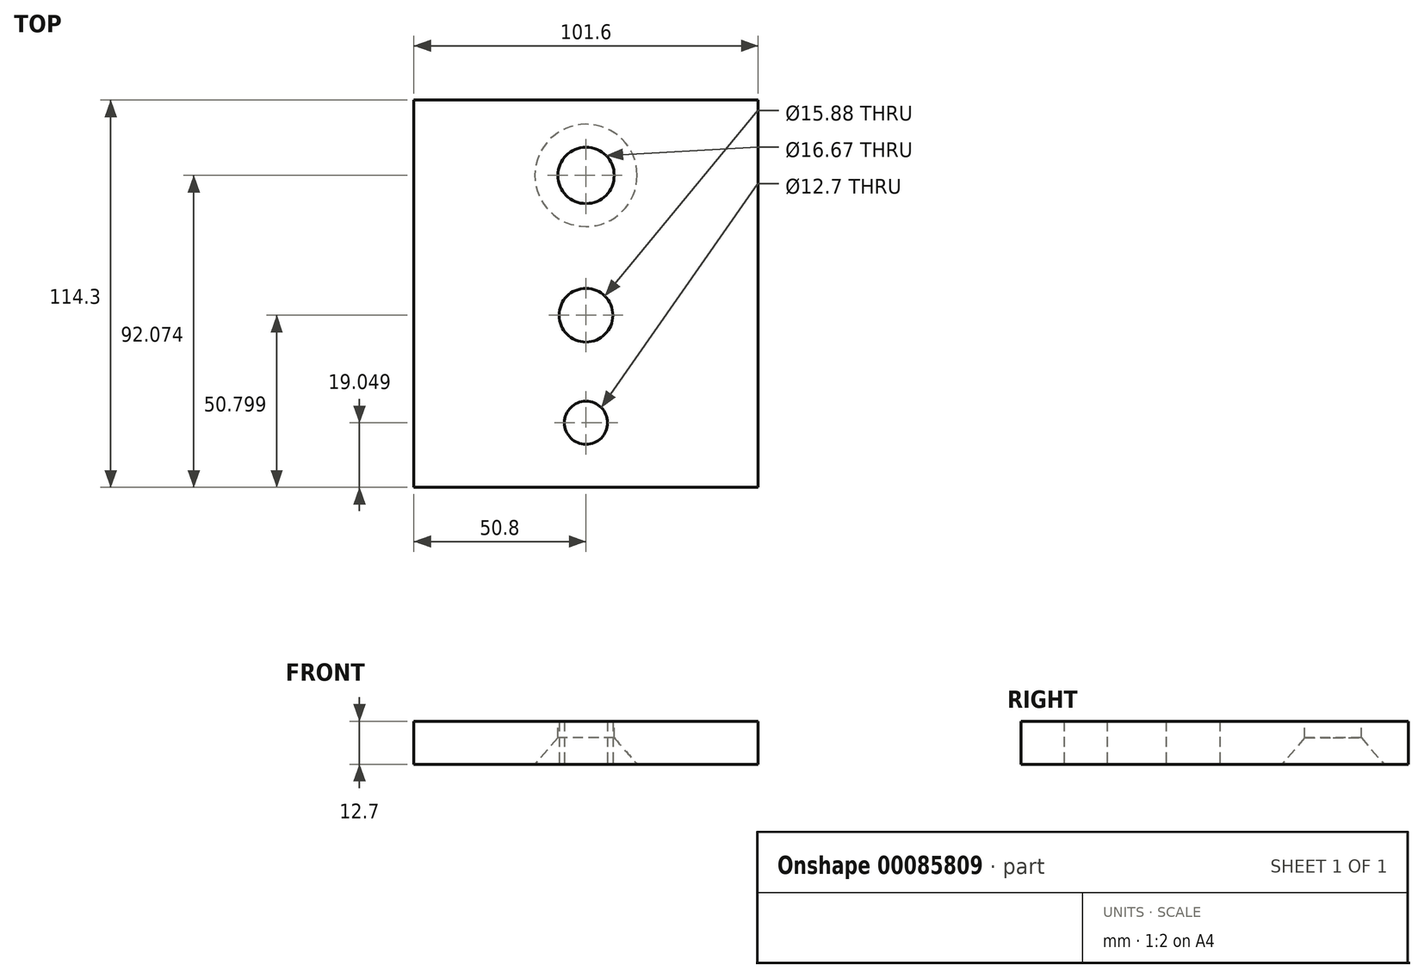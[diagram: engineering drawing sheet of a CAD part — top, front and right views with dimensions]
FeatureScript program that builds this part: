
annotation { "Feature Type Name" : "Feature", "Feature Type Description" : "" }
export const myFeature = defineFeature(function(context is Context, id is Id, definition is map)
    precondition{}
    {
        {
            var Q0;
            Q0=qCreatedBy(makeId("Top.planeOp"),FACE);
            var sketch = newSketch(context, id + "F0", { "sketchPlane" : qUnion([Q0])});
            skPoint(sketch, "E0", {"position": v(-53.4, 28.23) * mm});
            skPoint(sketch, "E1", {"position": v(-53.4, 25.06) * mm});
            skPoint(sketch, "E2", {"position": v(-53.4, 53.63) * mm});
            skPoint(sketch, "E3", {"position": v(-53.4, 12.36) * mm});
            skPoint(sketch, "E4", {"position": v(-53.4, -19.4) * mm});
            skPoint(sketch, "E5", {"position": v(-92.66, 25.06) * mm});
            skLineSegment(sketch, "E6", {"start": v(-7.45, 12.36) * mm, "end": v(-37.08, 12.36) * mm});
            skPoint(sketch, "E7", {"position": v(-23.18, 2.59) * mm});
            skPoint(sketch, "E8", {"position": v(-85.14, 12.36) * mm});
            skPoint(sketch, "E9", {"position": v(-78.42, -7.18) * mm});
            skPoint(sketch, "E10", {"position": v(-20.86, 37.76) * mm});
            skPoint(sketch, "E11", {"position": v(-12.12, 12.36) * mm});
            skLineSegment(sketch, "E12", {"start": v(-2.6, 12.36) * mm, "end": v(-2.6, 63.16) * mm});
            skLineSegment(sketch, "E13", {"start": v(-104.2, 63.16) * mm, "end": v(-104.2, -38.44) * mm});
            skLineSegment(sketch, "E14", {"start": v(-104.2, -38.44) * mm, "end": v(-2.6, -38.44) * mm});
            skLineSegment(sketch, "E15", {"start": v(-2.6, -38.44) * mm, "end": v(-2.6, 63.16) * mm});
            skCircle(sketch, "E16", {"center": v(-53.4, 53.63) * mm, "radius": 1.27 * mm});
            skCircle(sketch, "E17", {"center": v(-92.66, 25.06) * mm, "radius": 1.27 * mm});
            skCircle(sketch, "E18", {"center": v(-85.14, 12.36) * mm, "radius": 1.27 * mm});
            skCircle(sketch, "E19", {"center": v(-78.42, -7.18) * mm, "radius": 1.27 * mm});
            skCircle(sketch, "E20", {"center": v(-53.4, -19.4) * mm, "radius": 1.27 * mm});
            skCircle(sketch, "E21", {"center": v(-23.18, 2.59) * mm, "radius": 1.27 * mm});
            skCircle(sketch, "E22", {"center": v(-12.12, 12.36) * mm, "radius": 1.27 * mm});
            skCircle(sketch, "E23", {"center": v(-20.86, 37.76) * mm, "radius": 1.27 * mm});
            skCircle(sketch, "E24", {"center": v(-53.4, 12.36) * mm, "radius": 1.27 * mm});
            skLineSegment(sketch, "E25", {"start": v(-104.2, 75.86) * mm, "end": v(-2.6, 75.86) * mm});
            skLineSegment(sketch, "E26", {"start": v(-2.6, 63.16) * mm, "end": v(-2.6, 75.86) * mm});
            skLineSegment(sketch, "E27", {"start": v(-104.2, 63.16) * mm, "end": v(-104.2, 75.86) * mm});
            skSolve(sketch);
        }
        {
            var Q0;
            {var subQ0=sQuery(id+"F0.wireOp",EDGE,"oErOf9V9-PG69-BVOV-e9zF-uZxeaokeRpua");Q0=makeQuery(id+"F0.imprint","IMPRINT",FACE,{"disambiguationData":[TD([[makeQuery(id+"F0.imprint","IMPRINT",EDGE,{"derivedFrom":subQ0}),1.0]])]});}
            var Q1;
            Q1=makeQuery(id+"F0.imprint","IMPRINT",FACE,{"disambiguationData":[TD([[makeQuery(id+"F0.imprint","IMPRINT",EDGE,{"derivedFrom":sQuery(id+"F0.wireOp",EDGE,"E13")}),1.0]])]});
            var Q2;
            Q2=makeQuery(id+"F0.imprint","IMPRINT",FACE,{"disambiguationData":[TD([[makeQuery(id+"F0.imprint","IMPRINT",EDGE,{"derivedFrom":sQuery(id+"F0.wireOp",EDGE,"E17")}),1.0]])]});
            var Q3;
            Q3=makeQuery(id+"F0.imprint","IMPRINT",FACE,{"disambiguationData":[TD([[makeQuery(id+"F0.imprint","IMPRINT",EDGE,{"derivedFrom":sQuery(id+"F0.wireOp",EDGE,"E18")}),1.0]])]});
            var Q4;
            Q4=makeQuery(id+"F0.imprint","IMPRINT",FACE,{"disambiguationData":[TD([[makeQuery(id+"F0.imprint","IMPRINT",EDGE,{"derivedFrom":sQuery(id+"F0.wireOp",EDGE,"E19")}),1.0]])]});
            var Q5;
            Q5=makeQuery(id+"F0.imprint","IMPRINT",FACE,{"disambiguationData":[TD([[makeQuery(id+"F0.imprint","IMPRINT",EDGE,{"derivedFrom":sQuery(id+"F0.wireOp",EDGE,"E21")}),1.0]])]});
            var Q6;
            Q6=makeQuery(id+"F0.imprint","IMPRINT",FACE,{"disambiguationData":[TD([[makeQuery(id+"F0.imprint","IMPRINT",EDGE,{"derivedFrom":sQuery(id+"F0.wireOp",EDGE,"E23")}),1.0]])]});
            var Q7;
            {var subQ0=sQuery(id+"F0.wireOp",EDGE,"E22");var subQ1=sQuery(id+"F0.wireOp",EDGE,"E6");var subQ2=makeQuery(id+"F0.imprint","INTERSECT",VERTEX,{"disambiguationData":[OD(0.0)],"derivedFrom":[subQ1,subQ0]});Q7=makeQuery(id+"F0.imprint","IMPRINT",FACE,{"disambiguationData":[TD([[makeQuery(id+"F0.imprint","IMPRINT",EDGE,{"disambiguationData":[TD([[subQ2,1.0]])],"derivedFrom":subQ1}),1.0]])]});}
            var Q8;
            {var subQ0=sQuery(id+"F0.wireOp",EDGE,"E22");var subQ1=sQuery(id+"F0.wireOp",EDGE,"E6");var subQ2=makeQuery(id+"F0.imprint","INTERSECT",VERTEX,{"disambiguationData":[OD(0.0)],"derivedFrom":[subQ1,subQ0]});Q8=makeQuery(id+"F0.imprint","IMPRINT",FACE,{"disambiguationData":[TD([[makeQuery(id+"F0.imprint","IMPRINT",EDGE,{"disambiguationData":[TD([[subQ2,1.0]])],"derivedFrom":subQ1}),-1.0]])]});}
            extrude(context, id + "F1", {"entities" : qUnion([Q0, Q1, Q2, Q3, Q4, Q5, Q6, Q7, Q8]), "depth" : 12.7 * mm, "offsetDistance" : 25.4 * mm});
        }
        {
            var Q0;
            Q0=makeQuery(id+"F1.opExtrude","CAP_FACE",FACE,{"disambiguationData":[OSD([sQuery(id+"F0.wireOp",EDGE,"oErOf9V9-PG69-BVOV-e9zF-uZxeaokeRpua"),sQuery(id+"F0.wireOp",EDGE,"E13"),sQuery(id+"F0.wireOp",EDGE,"E14"),sQuery(id+"F0.wireOp",EDGE,"E15"),sQuery(id+"F0.wireOp",EDGE,"E16"),sQuery(id+"F0.wireOp",EDGE,"E17"),sQuery(id+"F0.wireOp",EDGE,"E18"),sQuery(id+"F0.wireOp",EDGE,"E19"),sQuery(id+"F0.wireOp",EDGE,"E20"),sQuery(id+"F0.wireOp",EDGE,"E21"),sQuery(id+"F0.wireOp",EDGE,"E22"),sQuery(id+"F0.wireOp",EDGE,"E23"),sQuery(id+"F0.wireOp",EDGE,"E24")])],"isStart":false});
            var sketch = newSketch(context, id + "F2", { "sketchPlane" : qUnion([Q0])});
            skPoint(sketch, "E28", {"position": v(-53.4, 53.63) * mm});
            skPoint(sketch, "E29", {"position": v(-20.86, 37.76) * mm});
            skPoint(sketch, "E30", {"position": v(-12.12, 12.36) * mm});
            skPoint(sketch, "E31", {"position": v(-23.18, 2.59) * mm});
            skPoint(sketch, "E32", {"position": v(-53.4, -19.4) * mm});
            skPoint(sketch, "E33", {"position": v(-78.42, -7.18) * mm});
            skPoint(sketch, "E34", {"position": v(-85.14, 12.36) * mm});
            skPoint(sketch, "E35", {"position": v(-92.66, 25.06) * mm});
            skPoint(sketch, "E36", {"position": v(-53.4, 12.36) * mm});
            skSolve(sketch);
        }
        {
            var Q0;
            Q0=sQuery(id+"F2.wireOp",VERTEX,"E36");
            var Q1;
            Q1=makeQuery(id+"F1.opExtrude","SWEPT_BODY",BODY,{"disambiguationData":[OSD([sQuery(id+"F0.wireOp",EDGE,"oErOf9V9-PG69-BVOV-e9zF-uZxeaokeRpua"),sQuery(id+"F0.wireOp",EDGE,"E13"),sQuery(id+"F0.wireOp",EDGE,"E14"),sQuery(id+"F0.wireOp",EDGE,"E15"),sQuery(id+"F0.wireOp",EDGE,"E16"),sQuery(id+"F0.wireOp",EDGE,"E17"),sQuery(id+"F0.wireOp",EDGE,"E18"),sQuery(id+"F0.wireOp",EDGE,"E19"),sQuery(id+"F0.wireOp",EDGE,"E20"),sQuery(id+"F0.wireOp",EDGE,"E21"),sQuery(id+"F0.wireOp",EDGE,"E22"),sQuery(id+"F0.wireOp",EDGE,"E23"),sQuery(id+"F0.wireOp",EDGE,"E24")])]});
            hole(context, id + "F3", {"style" : HoleStyle.SIMPLE, "endStyle" : HoleEndStyle.THROUGH, "holeDiameter" : 15.88 * mm, "majorDiameter" : 6.35 * mm, "tappedDepth" : 12.7 * mm, "tapClearance" : 3, "startFromSketch" : true, "locations" : qUnion([Q0]), "scope" : qUnion([Q1])});
        }
        {
            var Q0;
            Q0=makeQuery(id+"F1.opExtrude","CAP_FACE",FACE,{"disambiguationData":[OSD([sQuery(id+"F0.wireOp",EDGE,"oErOf9V9-PG69-BVOV-e9zF-uZxeaokeRpua"),sQuery(id+"F0.wireOp",EDGE,"E13"),sQuery(id+"F0.wireOp",EDGE,"E14"),sQuery(id+"F0.wireOp",EDGE,"E15"),sQuery(id+"F0.wireOp",EDGE,"E16"),sQuery(id+"F0.wireOp",EDGE,"E17"),sQuery(id+"F0.wireOp",EDGE,"E18"),sQuery(id+"F0.wireOp",EDGE,"E19"),sQuery(id+"F0.wireOp",EDGE,"E20"),sQuery(id+"F0.wireOp",EDGE,"E21"),sQuery(id+"F0.wireOp",EDGE,"E22"),sQuery(id+"F0.wireOp",EDGE,"E23"),sQuery(id+"F0.wireOp",EDGE,"E24")])],"isStart":true});
            var sketch = newSketch(context, id + "F4", { "sketchPlane" : qUnion([Q0])});
            skPoint(sketch, "E37", {"position": v(-53.4, -53.63) * mm});
            skSolve(sketch);
        }
        {
            var Q0;
            Q0=sQuery(id+"F4.wireOp",VERTEX,"E37");
            var Q1;
            Q1=makeQuery(id+"F1.opExtrude","SWEPT_BODY",BODY,{"disambiguationData":[OSD([sQuery(id+"F0.wireOp",EDGE,"oErOf9V9-PG69-BVOV-e9zF-uZxeaokeRpua"),sQuery(id+"F0.wireOp",EDGE,"E13"),sQuery(id+"F0.wireOp",EDGE,"E14"),sQuery(id+"F0.wireOp",EDGE,"E15"),sQuery(id+"F0.wireOp",EDGE,"E16"),sQuery(id+"F0.wireOp",EDGE,"E17"),sQuery(id+"F0.wireOp",EDGE,"E18"),sQuery(id+"F0.wireOp",EDGE,"E19"),sQuery(id+"F0.wireOp",EDGE,"E20"),sQuery(id+"F0.wireOp",EDGE,"E21"),sQuery(id+"F0.wireOp",EDGE,"E22"),sQuery(id+"F0.wireOp",EDGE,"E23"),sQuery(id+"F0.wireOp",EDGE,"E24")])]});
            hole(context, id + "F5", {"style" : HoleStyle.C_SINK, "endStyle" : HoleEndStyle.THROUGH, "standardTappedOrClearance" : lookupTablePath({ "fit" : "Free", "standard" : "ANSI", "size" : "5/8", "type" : "Clearance" }), "standardBlindInLast" : lookupTablePath({ "fit" : "Free", "standard" : "ANSI", "engagement" : "75%", "pitch" : "11 tpi", "size" : "5/8", "type" : "Clearance & tapped" }), "holeDiameter" : 16.67 * mm, "cSinkDiameter" : 30.18 * mm, "cSinkAngle" : 82 * degree, "majorDiameter" : 6.35 * mm, "tappedDepth" : 12.7 * mm, "tapClearance" : 3, "startFromSketch" : true, "locations" : qUnion([Q0]), "scope" : qUnion([Q1])});
        }
        {
            var Q0;
            Q0=makeQuery(id+"F1.opExtrude","CAP_FACE",FACE,{"disambiguationData":[OSD([sQuery(id+"F0.wireOp",EDGE,"oErOf9V9-PG69-BVOV-e9zF-uZxeaokeRpua"),sQuery(id+"F0.wireOp",EDGE,"E13"),sQuery(id+"F0.wireOp",EDGE,"E14"),sQuery(id+"F0.wireOp",EDGE,"E15"),sQuery(id+"F0.wireOp",EDGE,"E16"),sQuery(id+"F0.wireOp",EDGE,"E17"),sQuery(id+"F0.wireOp",EDGE,"E18"),sQuery(id+"F0.wireOp",EDGE,"E19"),sQuery(id+"F0.wireOp",EDGE,"E20"),sQuery(id+"F0.wireOp",EDGE,"E21"),sQuery(id+"F0.wireOp",EDGE,"E22"),sQuery(id+"F0.wireOp",EDGE,"E23"),sQuery(id+"F0.wireOp",EDGE,"E24")])],"isStart":false});
            var sketch = newSketch(context, id + "F6", { "sketchPlane" : qUnion([Q0])});
            skPoint(sketch, "E38", {"position": v(-53.4, -19.4) * mm});
            skSolve(sketch);
        }
        {
            var Q0;
            Q0=sQuery(id+"F6.wireOp",VERTEX,"E38");
            var Q1;
            Q1=makeQuery(id+"F1.opExtrude","SWEPT_BODY",BODY,{"disambiguationData":[OSD([sQuery(id+"F0.wireOp",EDGE,"oErOf9V9-PG69-BVOV-e9zF-uZxeaokeRpua"),sQuery(id+"F0.wireOp",EDGE,"E13"),sQuery(id+"F0.wireOp",EDGE,"E14"),sQuery(id+"F0.wireOp",EDGE,"E15"),sQuery(id+"F0.wireOp",EDGE,"E16"),sQuery(id+"F0.wireOp",EDGE,"E17"),sQuery(id+"F0.wireOp",EDGE,"E18"),sQuery(id+"F0.wireOp",EDGE,"E19"),sQuery(id+"F0.wireOp",EDGE,"E20"),sQuery(id+"F0.wireOp",EDGE,"E21"),sQuery(id+"F0.wireOp",EDGE,"E22"),sQuery(id+"F0.wireOp",EDGE,"E23"),sQuery(id+"F0.wireOp",EDGE,"E24")])]});
            hole(context, id + "F7", {"style" : HoleStyle.SIMPLE, "endStyle" : HoleEndStyle.THROUGH, "holeDiameter" : 12.7 * mm, "majorDiameter" : 6.35 * mm, "tappedDepth" : 12.7 * mm, "tapClearance" : 3, "startFromSketch" : true, "locations" : qUnion([Q0]), "scope" : qUnion([Q1])});
        }
    });
